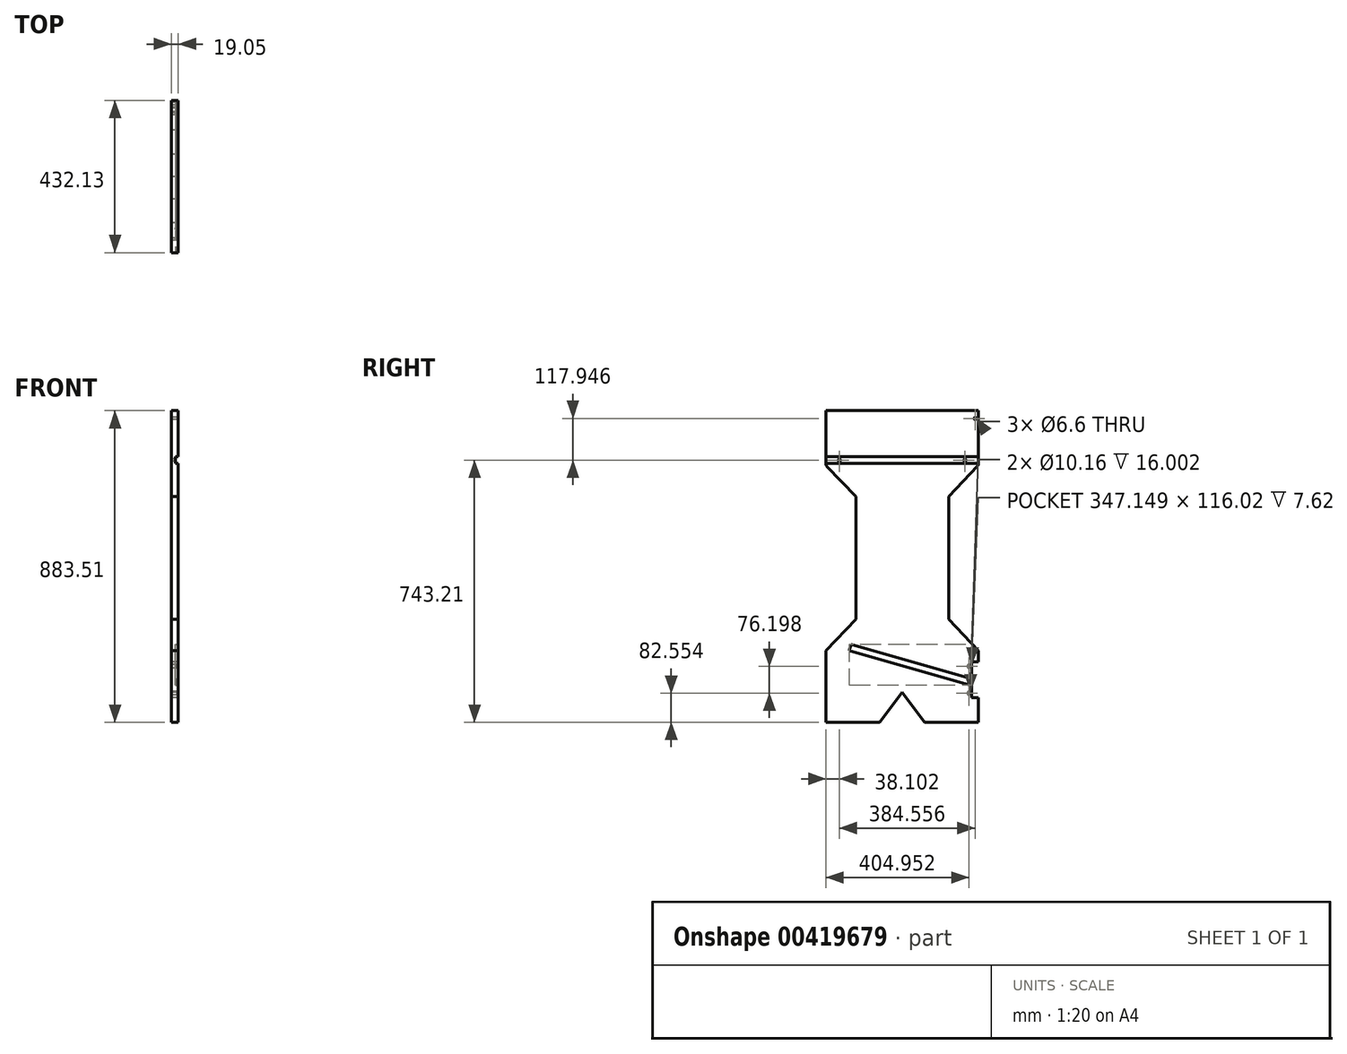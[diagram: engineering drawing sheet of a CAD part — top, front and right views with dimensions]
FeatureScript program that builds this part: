
annotation { "Feature Type Name" : "Feature", "Feature Type Description" : "" }
export const myFeature = defineFeature(function(context is Context, id is Id, definition is map)
    precondition{}
    {
        {
            var Q0;
            Q0=qCreatedBy(makeId("Right.planeOp"),FACE);
            var sketch = newSketch(context, id + "F0", { "sketchPlane" : qUnion([Q0])});
            skLineSegment(sketch, "E0.bottom", {"start": v(215.57, 77.66) * mm, "end": v(-216.23, 77.66) * mm});
            skLineSegment(sketch, "E0.left", {"start": v(215.57, 77.66) * mm, "end": v(215.57, -73.15) * mm});
            skLineSegment(sketch, "E0.right", {"start": v(-216.23, 77.66) * mm, "end": v(-216.23, -73.15) * mm});
            skPoint(sketch, "E0.middle", {"position": v(0, 0) * mm});
            skLineSegment(sketch, "E1", {"start": v(-213.41, -80.17) * mm, "end": v(-131.54, -165.77) * mm});
            skLineSegment(sketch, "E2", {"start": v(212.78, -80.14) * mm, "end": v(131.54, -165.77) * mm});
            skLineSegment(sketch, "E3", {"start": v(-131.54, -165.77) * mm, "end": v(-131.54, -513.75) * mm});
            skArc(sketch, "E4.filletArc", {"start": v(-216.23, -73.15) * mm, "mid": v(-215.5, -76.93) * mm, "end": v(-213.41, -80.17) * mm});
            skArc(sketch, "E5.filletArc", {"start": v(212.78, -80.14) * mm, "mid": v(214.85, -76.91) * mm, "end": v(215.57, -73.15) * mm});
            skLineSegment(sketch, "E6", {"start": v(-131.54, -513.75) * mm, "end": v(-215.9, -602.65) * mm});
            skLineSegment(sketch, "E7", {"start": v(-215.9, -602.65) * mm, "end": v(-215.9, -805.85) * mm});
            skLineSegment(sketch, "E8.MirrorCS", {"start": v(131.54, -165.77) * mm, "end": v(131.54, -513.75) * mm});
            skLineSegment(sketch, "E9.MirrorCS", {"start": v(131.54, -513.75) * mm, "end": v(215.9, -602.65) * mm});
            skLineSegment(sketch, "E10", {"start": v(-131.54, -165.77) * mm, "end": v(-34.69, -165.77) * mm, "construction": true});
            skLineSegment(sketch, "E11", {"start": v(-215.9, -602.65) * mm, "end": v(-131.54, -602.65) * mm, "construction": true});
            skLineSegment(sketch, "E12", {"start": v(-215.9, -805.85) * mm, "end": v(-63.5, -805.85) * mm});
            skLineSegment(sketch, "E13", {"start": v(-63.5, -805.85) * mm, "end": v(0, -721.49) * mm});
            skLineSegment(sketch, "E14", {"start": v(0, -721.49) * mm, "end": v(63.5, -805.85) * mm});
            skLineSegment(sketch, "E15", {"start": v(63.5, -805.85) * mm, "end": v(215.9, -805.85) * mm});
            skPoint(sketch, "E16", {"position": v(215.9, -634.4) * mm});
            skPoint(sketch, "E17", {"position": v(215.9, -736) * mm});
            skLineSegment(sketch, "E18", {"start": v(215.9, -634.4) * mm, "end": v(196.85, -634.4) * mm});
            skLineSegment(sketch, "E19", {"start": v(196.85, -634.4) * mm, "end": v(196.85, -736) * mm});
            skLineSegment(sketch, "E20", {"start": v(196.85, -736) * mm, "end": v(215.9, -736) * mm});
            skLineSegment(sketch, "E21", {"start": v(215.9, -602.65) * mm, "end": v(215.9, -634.4) * mm});
            skLineSegment(sketch, "E22", {"start": v(215.9, -736) * mm, "end": v(215.9, -805.85) * mm});
            skSolve(sketch);
        }
        {
            var Q0;
            Q0=qSketchRegion(id+"F0",true);
            extrude(context, id + "F1", {"entities" : qUnion([Q0]), "depth" : 19.05 * mm});
        }
        {
            var Q0;
            Q0=makeQuery(id+"F1.opExtrude","CAP_FACE",FACE,{"disambiguationData":[OSD([sQuery(id+"F0.wireOp",EDGE,"E0.bottom"),sQuery(id+"F0.wireOp",EDGE,"E0.left"),sQuery(id+"F0.wireOp",EDGE,"E0.right"),sQuery(id+"F0.wireOp",EDGE,"E1"),sQuery(id+"F0.wireOp",EDGE,"E2"),sQuery(id+"F0.wireOp",EDGE,"E3"),sQuery(id+"F0.wireOp",EDGE,"E4.filletArc"),sQuery(id+"F0.wireOp",EDGE,"E5.filletArc"),sQuery(id+"F0.wireOp",EDGE,"E6"),sQuery(id+"F0.wireOp",EDGE,"E7"),sQuery(id+"F0.wireOp",EDGE,"E8.MirrorCS"),sQuery(id+"F0.wireOp",EDGE,"E9.MirrorCS"),sQuery(id+"F0.wireOp",EDGE,"E12"),sQuery(id+"F0.wireOp",EDGE,"E13"),sQuery(id+"F0.wireOp",EDGE,"E14"),sQuery(id+"F0.wireOp",EDGE,"E15"),sQuery(id+"F0.wireOp",EDGE,"E18"),sQuery(id+"F0.wireOp",EDGE,"E19"),sQuery(id+"F0.wireOp",EDGE,"E20"),sQuery(id+"F0.wireOp",EDGE,"E21"),sQuery(id+"F0.wireOp",EDGE,"E22")])],"isStart":false});
            var sketch = newSketch(context, id + "F2", { "sketchPlane" : qUnion([Q0])});
            skLineSegment(sketch, "E23", {"start": v(196.84, -682.6) * mm, "end": v(191.6, -700.92) * mm});
            skLineSegment(sketch, "E24", {"start": v(191.6, -700.92) * mm, "end": v(-150.3, -603.22) * mm});
            skLineSegment(sketch, "E25", {"start": v(-150.3, -603.22) * mm, "end": v(-145.07, -584.9) * mm});
            skLineSegment(sketch, "E26", {"start": v(196.84, -682.6) * mm, "end": v(-145.07, -584.9) * mm});
            skSolve(sketch);
        }
        {
            var Q0;
            Q0=makeQuery(id+"F2.imprint","IMPRINT",FACE,{"disambiguationData":[TD([[makeQuery(id+"F2.imprint","IMPRINT",EDGE,{"derivedFrom":sQuery(id+"F2.wireOp",EDGE,"E23")}),-1.0]])]});
            extrude(context, id + "F3", {"entities" : qUnion([Q0]), "operationType" : NewBodyOperationType.REMOVE, "oppositeDirection" : true, "depth" : 7.62 * mm});
        }
        {
            var Q0;
            Q0=makeQuery(id+"F2.imprint","IMPRINT",FACE,{"disambiguationData":[TD([[makeQuery(id+"F2.imprint","IMPRINT",EDGE,{"derivedFrom":sQuery(id+"F2.wireOp",EDGE,"E23")}),1.0]])]});
            var sketch = newSketch(context, id + "F4", { "sketchPlane" : qUnion([Q0])});
            skLineSegment(sketch, "E27", {"start": v(216.17, -71.28) * mm, "end": v(-216.23, -71.28) * mm});
            skLineSegment(sketch, "E28", {"start": v(-216.23, -71.28) * mm, "end": v(-216.23, -52.23) * mm});
            skLineSegment(sketch, "E29", {"start": v(-216.23, -52.23) * mm, "end": v(215.57, -52.23) * mm});
            skLineSegment(sketch, "E30", {"start": v(215.57, -52.23) * mm, "end": v(216.17, -71.28) * mm});
            skSolve(sketch);
        }
        {
            var Q0;
            Q0=qSketchRegion(id+"F4",true);
            extrude(context, id + "F5", {"entities" : qUnion([Q0]), "operationType" : NewBodyOperationType.REMOVE, "oppositeDirection" : true, "depth" : 7.62 * mm});
        }
        {
            var Q0;
            Q0=makeQuery(id+"F0.imprint","IMPRINT",FACE,{"disambiguationData":[TD([[makeQuery(id+"F0.imprint","IMPRINT",EDGE,{"derivedFrom":sQuery(id+"F0.wireOp",EDGE,"E0.bottom")}),1.0]])]});
            var sketch = newSketch(context, id + "F6", { "sketchPlane" : qUnion([Q0])});
            skCircle(sketch, "E31", {"center": v(-178.13, -62.64) * mm, "radius": 3.3 * mm});
            skCircle(sketch, "E32", {"center": v(177.47, -62.64) * mm, "radius": 3.3 * mm});
            skCircle(sketch, "E33", {"center": v(206.43, 55.3) * mm, "radius": 3.3 * mm});
            skSolve(sketch);
        }
        {
            var Q0;
            Q0 = qSketchRegion(id + "F6", true);
            extrude(context, id + "F7", {"entities" : qUnion([Q0]), "operationType" : NewBodyOperationType.REMOVE, "depth" : 19.05 * mm});
        }
        {
            var Q0;
            Q0=makeQuery(id+"F0.imprint","IMPRINT",FACE,{"disambiguationData":[TD([[makeQuery(id+"F0.imprint","IMPRINT",EDGE,{"derivedFrom":sQuery(id+"F0.wireOp",EDGE,"E0.bottom")}),1.0]])]});
            var sketch = newSketch(context, id + "F8", { "sketchPlane" : qUnion([Q0])});
            skPoint(sketch, "E34", {"position": v(196.85, -634.4) * mm});
            skPoint(sketch, "E35", {"position": v(196.85, -736) * mm});
            skLineSegment(sketch, "E36", {"start": v(196.85, -634.4) * mm, "end": v(188.72, -634.4) * mm, "construction": true});
            skLineSegment(sketch, "E37", {"start": v(188.72, -634.4) * mm, "end": v(188.72, -647.1) * mm, "construction": true});
            skLineSegment(sketch, "E38", {"start": v(196.85, -736) * mm, "end": v(188.72, -736) * mm, "construction": true});
            skLineSegment(sketch, "E39", {"start": v(188.72, -736) * mm, "end": v(188.72, -723.3) * mm, "construction": true});
            skCircle(sketch, "E40", {"center": v(188.72, -723.3) * mm, "radius": 5.08 * mm});
            skCircle(sketch, "E41", {"center": v(188.72, -647.1) * mm, "radius": 5.08 * mm});
            skSolve(sketch);
        }
        {
            var Q0;
            Q0 = qSketchRegion(id + "F8", true);
            extrude(context, id + "F9", {"entities" : qUnion([Q0]), "operationType" : NewBodyOperationType.REMOVE, "depth" : 16 * mm});
        }
    });
